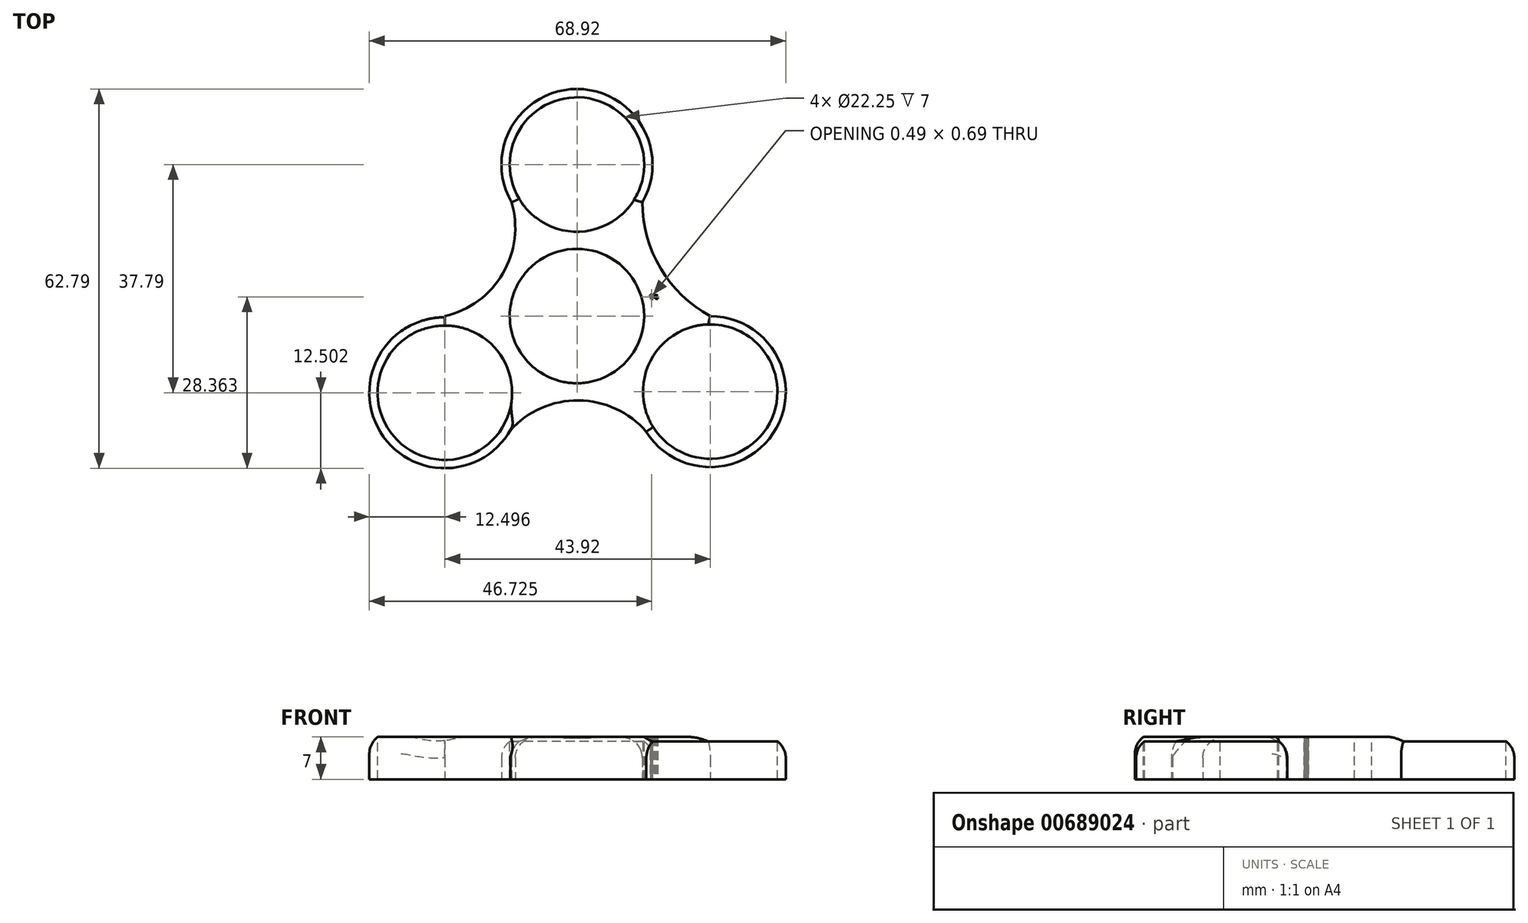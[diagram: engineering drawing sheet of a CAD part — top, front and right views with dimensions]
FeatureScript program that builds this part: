
annotation { "Feature Type Name" : "Feature", "Feature Type Description" : "" }
export const myFeature = defineFeature(function(context is Context, id is Id, definition is map)
    precondition{}
    {
        {
            var Q0;
            Q0=qCreatedBy(makeId("Top.planeOp"),FACE);
            var sketch = newSketch(context, id + "F0", { "sketchPlane" : qUnion([Q0])});
            skCircle(sketch, "E0", {"center": v(0, 0) * mm, "radius": 11.12 * mm});
            skCircle(sketch, "E1", {"center": v(0, 25.25) * mm, "radius": 11.12 * mm});
            skCircle(sketch, "E2", {"center": v(-21.87, -12.63) * mm, "radius": 11.12 * mm});
            skCircle(sketch, "E3", {"center": v(21.87, -12.62) * mm, "radius": 11.12 * mm});
            skSolve(sketch);
        }
        {
            var Q0;
            Q0=qCreatedBy(makeId("Top.planeOp"),FACE);
            var sketch = newSketch(context, id + "F1", { "sketchPlane" : qUnion([Q0])});
            skArc(sketch, "E4", {"start": v(-21.86, -0.2) * mm, "mid": v(-32.69, -18.95) * mm, "end": v(-11.04, -18.95) * mm});
            skArc(sketch, "E5", {"start": v(11.23, -18.76) * mm, "mid": v(32.88, -18.76) * mm, "end": v(22.06, 0) * mm});
            skArc(sketch, "E6", {"start": v(10.83, 18.84) * mm, "mid": v(0, 37.6) * mm, "end": v(-10.83, 18.84) * mm});
            skLineSegment(sketch, "E7", {"start": v(0, 25.1) * mm, "end": v(0, 37.6) * mm});
            skLineSegment(sketch, "E8", {"start": v(-21.86, -0.2) * mm, "end": v(-21.86, 0) * mm});
            skLineSegment(sketch, "E9", {"start": v(-11.04, -18.95) * mm, "end": v(-10.65, -19.17) * mm});
            skLineSegment(sketch, "E10", {"start": v(11.23, -18.76) * mm, "end": v(11.15, -18.8) * mm});
            skArc(sketch, "E11", {"start": v(-21.86, 0) * mm, "mid": v(-12.28, 7.04) * mm, "end": v(-10.83, 18.84) * mm});
            skArc(sketch, "E12", {"start": v(10.83, 18.84) * mm, "mid": v(13.86, 7.88) * mm, "end": v(22.06, 0) * mm});
            skArc(sketch, "E13", {"start": v(11.48, -19.17) * mm, "mid": v(0.27, -13.97) * mm, "end": v(-11.04, -18.95) * mm});
            skPoint(sketch, "E13.startSnap0", {"position": v(-10.65, -19.17) * mm});
            skPoint(sketch, "E14.orphan", {"position": v(0.55, -25.64) * mm});
            skPoint(sketch, "E15.orphan", {"position": v(-21.86, 9.68) * mm});
            skSolve(sketch);
        }
        {
            var Q0;
            Q0 = qSketchRegion(id + "F1", true);
            extrude(context, id + "F2", {"entities" : qUnion([Q0]), "depth" : 7 * mm, "offsetDistance" : 25 * mm});
        }
        {
            var Q0;
            Q0 = qSketchRegion(id + "F0", true);
            extrude(context, id + "F3", {"entities" : qUnion([Q0]), "operationType" : NewBodyOperationType.REMOVE, "oppositeDirection" : true, "depth" : 25 * mm, "offsetDistance" : 25 * mm});
        }
        {
            var Q0;
            Q0=makeQuery(id+"F2.opExtrude","CAP_FACE",FACE,{"disambiguationData":[OSD([sQuery(id+"F1.wireOp",EDGE,"E4"),sQuery(id+"F1.wireOp",EDGE,"E5"),sQuery(id+"F1.wireOp",EDGE,"E6"),sQuery(id+"F1.wireOp",EDGE,"E8"),sQuery(id+"F1.wireOp",EDGE,"E11"),sQuery(id+"F1.wireOp",EDGE,"E12"),sQuery(id+"F1.wireOp",EDGE,"E13")])],"isStart":false});
            var sketch = newSketch(context, id + "F4", { "sketchPlane" : qUnion([Q0])});
            skCircle(sketch, "E16", {"center": v(-21.86, -12.7) * mm, "radius": 11.12 * mm});
            skSolve(sketch);
        }
        {
            var Q0;
            Q0 = qSketchRegion(id + "F4", true);
            extrude(context, id + "F5", {"entities" : qUnion([Q0]), "operationType" : NewBodyOperationType.REMOVE, "oppositeDirection" : true, "depth" : 7 * mm, "offsetDistance" : 25 * mm});
        }
        {
            var Q0;
            Q0=makeQuery(id+"F2.opExtrude","CAP_FACE",FACE,{"disambiguationData":[OSD([sQuery(id+"F1.wireOp",EDGE,"E4"),sQuery(id+"F1.wireOp",EDGE,"E5"),sQuery(id+"F1.wireOp",EDGE,"E6"),sQuery(id+"F1.wireOp",EDGE,"E8"),sQuery(id+"F1.wireOp",EDGE,"E11"),sQuery(id+"F1.wireOp",EDGE,"E12"),sQuery(id+"F1.wireOp",EDGE,"E13")])],"isStart":false});
            var sketch = newSketch(context, id + "F6", { "sketchPlane" : qUnion([Q0])});
            skCircle(sketch, "E17", {"center": v(0, 25.1) * mm, "radius": 11.12 * mm});
            skSolve(sketch);
        }
        {
            var Q0;
            Q0 = qSketchRegion(id + "F6", true);
            extrude(context, id + "F7", {"entities" : qUnion([Q0]), "operationType" : NewBodyOperationType.REMOVE, "oppositeDirection" : true, "depth" : 25 * mm, "offsetDistance" : 25 * mm});
        }
        {
            var Q0;
            Q0=makeQuery(id+"F2.opExtrude","CAP_FACE",FACE,{"disambiguationData":[OSD([sQuery(id+"F1.wireOp",EDGE,"E4"),sQuery(id+"F1.wireOp",EDGE,"E5"),sQuery(id+"F1.wireOp",EDGE,"E6"),sQuery(id+"F1.wireOp",EDGE,"E8"),sQuery(id+"F1.wireOp",EDGE,"E11"),sQuery(id+"F1.wireOp",EDGE,"E12"),sQuery(id+"F1.wireOp",EDGE,"E13")])],"isStart":false});
            var sketch = newSketch(context, id + "F8", { "sketchPlane" : qUnion([Q0])});
            skCircle(sketch, "E18", {"center": v(22.06, -12.5) * mm, "radius": 11.12 * mm});
            skSolve(sketch);
        }
        {
            var Q0;
            Q0 = qSketchRegion(id + "F8", true);
            extrude(context, id + "F9", {"entities" : qUnion([Q0]), "operationType" : NewBodyOperationType.REMOVE, "oppositeDirection" : true, "depth" : 25 * mm, "offsetDistance" : 25 * mm});
        }
        {
            var Q0;
            Q0=makeQuery(id+"F2.opExtrude","CAP_FACE",FACE,{"disambiguationData":[OSD([sQuery(id+"F1.wireOp",EDGE,"E4"),sQuery(id+"F1.wireOp",EDGE,"E5"),sQuery(id+"F1.wireOp",EDGE,"E6"),sQuery(id+"F1.wireOp",EDGE,"E8"),sQuery(id+"F1.wireOp",EDGE,"E11"),sQuery(id+"F1.wireOp",EDGE,"E12"),sQuery(id+"F1.wireOp",EDGE,"E13")])],"isStart":false});
            var sketch = newSketch(context, id + "F10", { "sketchPlane" : qUnion([Q0])});
            skCircle(sketch, "E19", {"center": v(0, 0) * mm, "radius": 11.12 * mm});
            skSolve(sketch);
        }
        {
            var Q0;
            Q0 = qSketchRegion(id + "F10", true);
            extrude(context, id + "F11", {"entities" : qUnion([Q0]), "operationType" : NewBodyOperationType.REMOVE, "oppositeDirection" : true, "depth" : 25 * mm, "offsetDistance" : 25 * mm});
        }
        {
            var Q0;
            Q0=makeQuery(id+"F2.opExtrude","CAP_EDGE",EDGE,{"disambiguationData":[OSD([sQuery(id+"F1.wireOp",EDGE,"E6")])],"isStart":false});
            var Q1;
            Q1=makeQuery(id+"F2.opExtrude","CAP_EDGE",EDGE,{"disambiguationData":[OSD([sQuery(id+"F1.wireOp",EDGE,"E11")])],"isStart":false});
            var Q2;
            Q2=makeQuery(id+"F2.opExtrude","CAP_EDGE",EDGE,{"disambiguationData":[OSD([sQuery(id+"F1.wireOp",EDGE,"E13")])],"isStart":false});
            var Q3;
            Q3=makeQuery(id+"F2.opExtrude","CAP_EDGE",EDGE,{"disambiguationData":[OSD([sQuery(id+"F1.wireOp",EDGE,"E5")])],"isStart":false});
            var Q4;
            Q4=makeQuery(id+"F2.opExtrude","CAP_EDGE",EDGE,{"disambiguationData":[OSD([sQuery(id+"F1.wireOp",EDGE,"E12")])],"isStart":false});
            fillet(context, id + "F12", {"entities" : qUnion([Q0, Q1, Q2, Q3, Q4]), "radius" : 3.5 * mm, "tangentPropagation" : true, "allowEdgeOverflow" : false});
        }
        {
            var Q0;
            Q0=makeQuery(id+"F2.opExtrude","CAP_EDGE",EDGE,{"disambiguationData":[OSD([sQuery(id+"F1.wireOp",EDGE,"E4")])],"isStart":false});
            fillet(context, id + "F13", {"entities" : qUnion([Q0]), "radius" : 3.5 * mm, "tangentPropagation" : true, "allowEdgeOverflow" : false});
        }
        {
            var Q0;
            Q0=makeQuery(id+"F2.opExtrude","CAP_FACE",FACE,{"disambiguationData":[OSD([sQuery(id+"F1.wireOp",EDGE,"E4"),sQuery(id+"F1.wireOp",EDGE,"E5"),sQuery(id+"F1.wireOp",EDGE,"E6"),sQuery(id+"F1.wireOp",EDGE,"E8"),sQuery(id+"F1.wireOp",EDGE,"E11"),sQuery(id+"F1.wireOp",EDGE,"E12"),sQuery(id+"F1.wireOp",EDGE,"E13")])],"isStart":true});
            var sketch = newSketch(context, id + "F14", { "sketchPlane" : qUnion([Q0])});
            skText(sketch, "E20", { "text": "S E", "fontName": "OpenSans-BoldItalic.ttf"});
            const initialGuessF14  = {"E20": [0.0121, -0.0035, 1, 0, 0.00068]};
            skSetInitialGuess(sketch, initialGuessF14);
            skSolve(sketch);
        }
        {
            var Q0;
            Q0 = qSketchRegion(id + "F14", true);
            extrude(context, id + "F15", {"entities" : qUnion([Q0]), "operationType" : NewBodyOperationType.REMOVE, "oppositeDirection" : true, "depth" : 25 * mm, "offsetDistance" : 25 * mm});
        }
    });
